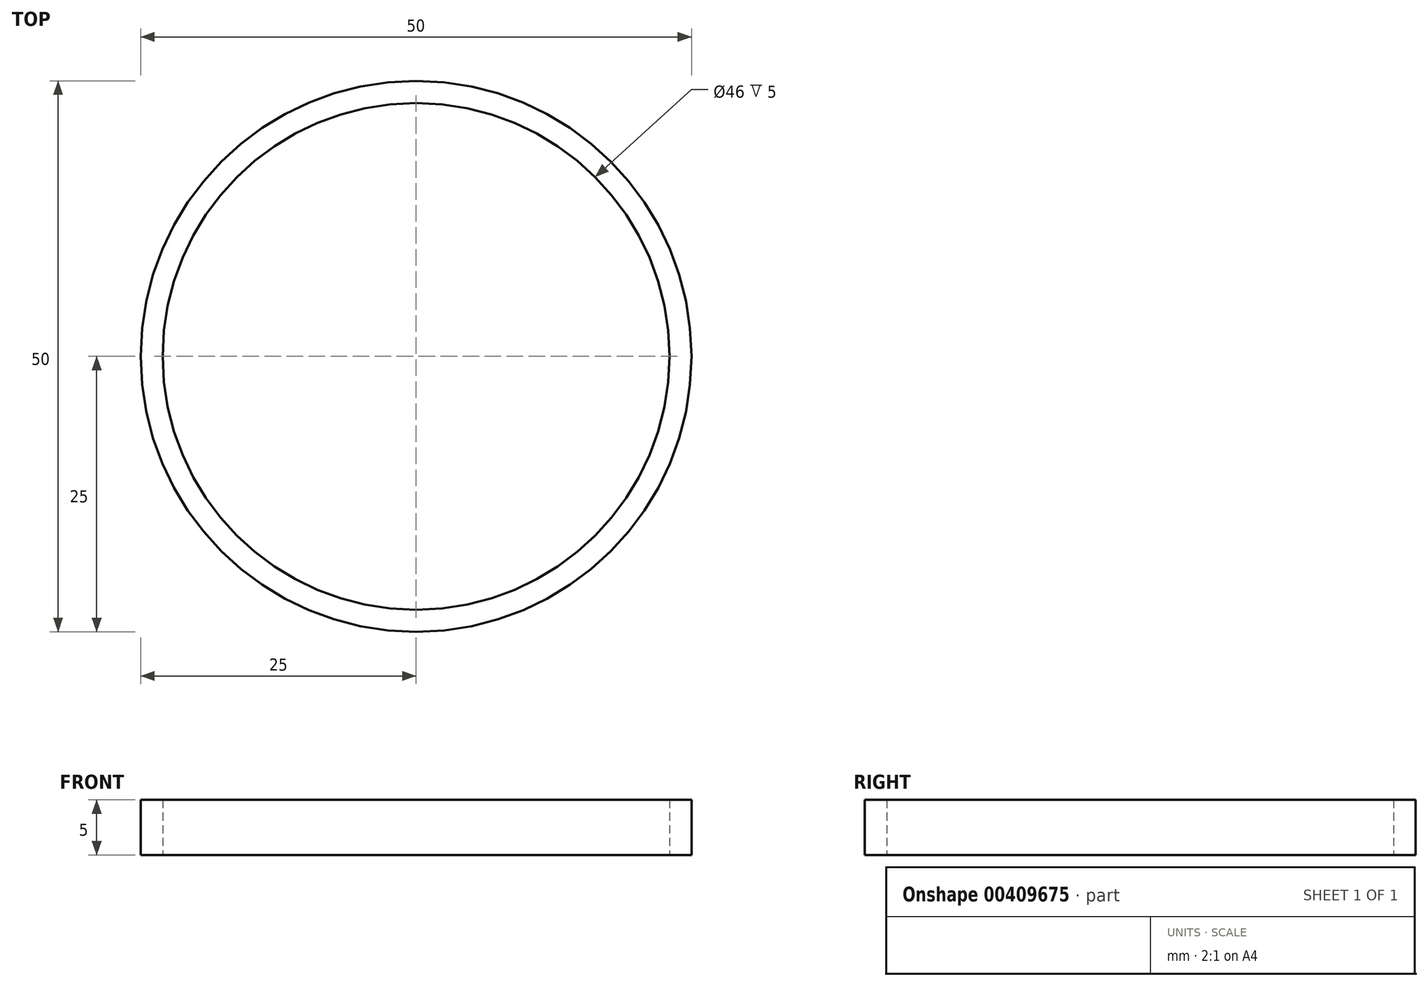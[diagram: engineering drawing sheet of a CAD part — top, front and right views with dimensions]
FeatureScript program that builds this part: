
annotation { "Feature Type Name" : "Feature", "Feature Type Description" : "" }
export const myFeature = defineFeature(function(context is Context, id is Id, definition is map)
    precondition{}
    {
        {
            var Q0;
            Q0=qCreatedBy(makeId("Top.planeOp"),FACE);
            var sketch = newSketch(context, id + "F0", { "sketchPlane" : qUnion([Q0])});
            skCircle(sketch, "E0", {"center": v(0, 0) * mm, "radius": 25 * mm});
            skCircle(sketch, "E1", {"center": v(0, 0) * mm, "radius": 23 * mm});
            skSolve(sketch);
        }
        {
            var Q0;
            Q0=makeQuery(id+"F0.imprint","IMPRINT",FACE,{"disambiguationData":[TD([[makeQuery(id+"F0.imprint","IMPRINT",EDGE,{"derivedFrom":sQuery(id+"F0.wireOp",EDGE,"E0")}),1.0]])]});
            extrude(context, id + "F1", {"entities" : qUnion([Q0]), "depth" : 5 * mm});
        }
    });
